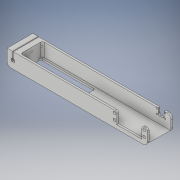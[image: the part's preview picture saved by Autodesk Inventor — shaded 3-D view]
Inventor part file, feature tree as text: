
AUTODESK INVENTOR PART (.ipt)
format: ipt  version: 2017 (Build 210142000, 142)  size: 331,776 bytes
history: native  units: in
note: dims shown in document units (in); Inventor stores cm internally (conversion verified against a paired STEP export)
features: sketch x8, extrude x6, projected_geometry x6, fillet x5, hole x2
ambient origin geometry x8: Origin, YZ Plane, XZ Plane, XY Plane, X Axis, Y Axis, Z Axis, Center Point
bodies: Solid1 (feature_tree)
feature tree (27):
  extrude  "Extrusion1"  Depth=1.685in
  extrude  "Extrusion2"  Depth=1.435in
  extrude  "Extrusion4"  Depth=0.125in TaperAngle=0.0deg
  extrude  "Extrusion5"  Depth=1.0in
  hole  "Hole1"  [1 undecoded]
  hole  "Hole2"  [1 undecoded]
  fillet  "Fillet1"  Radius=0.164in
  fillet  "Fillet2"  Radius=0.3937in
  fillet  "Fillet3"  Radius=0.19in
  extrude  "Extrusion6"  Depth=0.5in TaperAngle=0.0deg
  fillet  "Fillet4"  Radius=0.75in
  extrude  "Extrusion7"  Depth=0.1in
  fillet  "Fillet5"  Radius=0.078in
  sketch  "Sketch1"  dims[d0=1.0in d1=1.685in]
  sketch  "Sketch2"  dims[d2=0.875in d3=1.435in]
  projected_geometry  "Projected Loop1"
  sketch  "Sketch4"  dims[d4=0.125in d5=9.197in d6=0.0in]
  projected_geometry  "Projected Loop3"
  sketch  "Sketch5"  dims[d7=0.35in d8=1.0in]
  sketch  "Sketch6"  dims[d9=0.75in d10=2.0in]
  projected_geometry  "Projected Loop4"
  sketch  "Sketch7"  dims[d11=0.19in d12=0.19in d13=0.164in d14=0.3937in d15=0.19in]
  projected_geometry  "Projected Loop5"
  sketch  "Sketch9"  dims[d16=0.19in d19=0.5in d20=0.0in d26=0.75in]
  projected_geometry  "Projected Loop7"
  sketch  "Sketch10"  dims[d27=0.133in d28=0.078in d29=0.078in d30=0.098in d31=0.236in d32=0.0665in d33=0.0665in d34=0.0665in d35=0.0in d36=0.118in d37=0.133in d38=1.0in d39=0.5in d40=0.375in d41=0.05in d42=0.35in d43=1.685in d44=0.0in d45=0.75in d46=0.078in d47=0.078in d48=0.098in d49=0.0665in d50=0.0665in d51=0.0665in d52=0.0in d53=0.133in d54=1.0in d55=0.5in d56=0.375in d57=0.35in d58=0.133in d59=0.05in d60=1.685in d61=0.0in d62=0.25in d63=0.25in d64=1.685in d65=0.25in d66=0.8425in d67=0.2106in d68=0.2106in d69=0.158in d70=0.75in d71=0.375in d72=0.25in d73=0.5635in d74=0.355in d75=0.8108in d76=0.104in d77=0.276in d78=0.375in d79=0.25in d80=0.5635in d81=0.432in d82=0.8108in d83=0.125in d91=1.9488in d92=1.9488in d93=0.164in d95=0.3937in d96=0.197in d97=0.197in d105=0.25in d106=0.125in d107=1.685in d108=8.697in d109=0.5in d110=0.25in d111=1.185in d112=3.5985in d113=1.0in d114=0.0in d119=0.125in d121=0.774in d122=0.546in d125=0.3937in d126=1.0in d127=0.4229in d128=0.0969in d129=0.0969in d130=0.0in d131=0.621in d132=0.376in d133=0.25in d134=0.0in d135=0.0761in d136=0.0969in d137=0.0969in d138=0.376in d139=0.936in d140=0.936in d141=0.1in]
  projected_geometry  "Projected Loop8"
note: 2 required parameter values undecoded (feature->parameter linkage not recoverable at this tier; creation-order binding heuristic only, values carry confidence <= 0.55)
